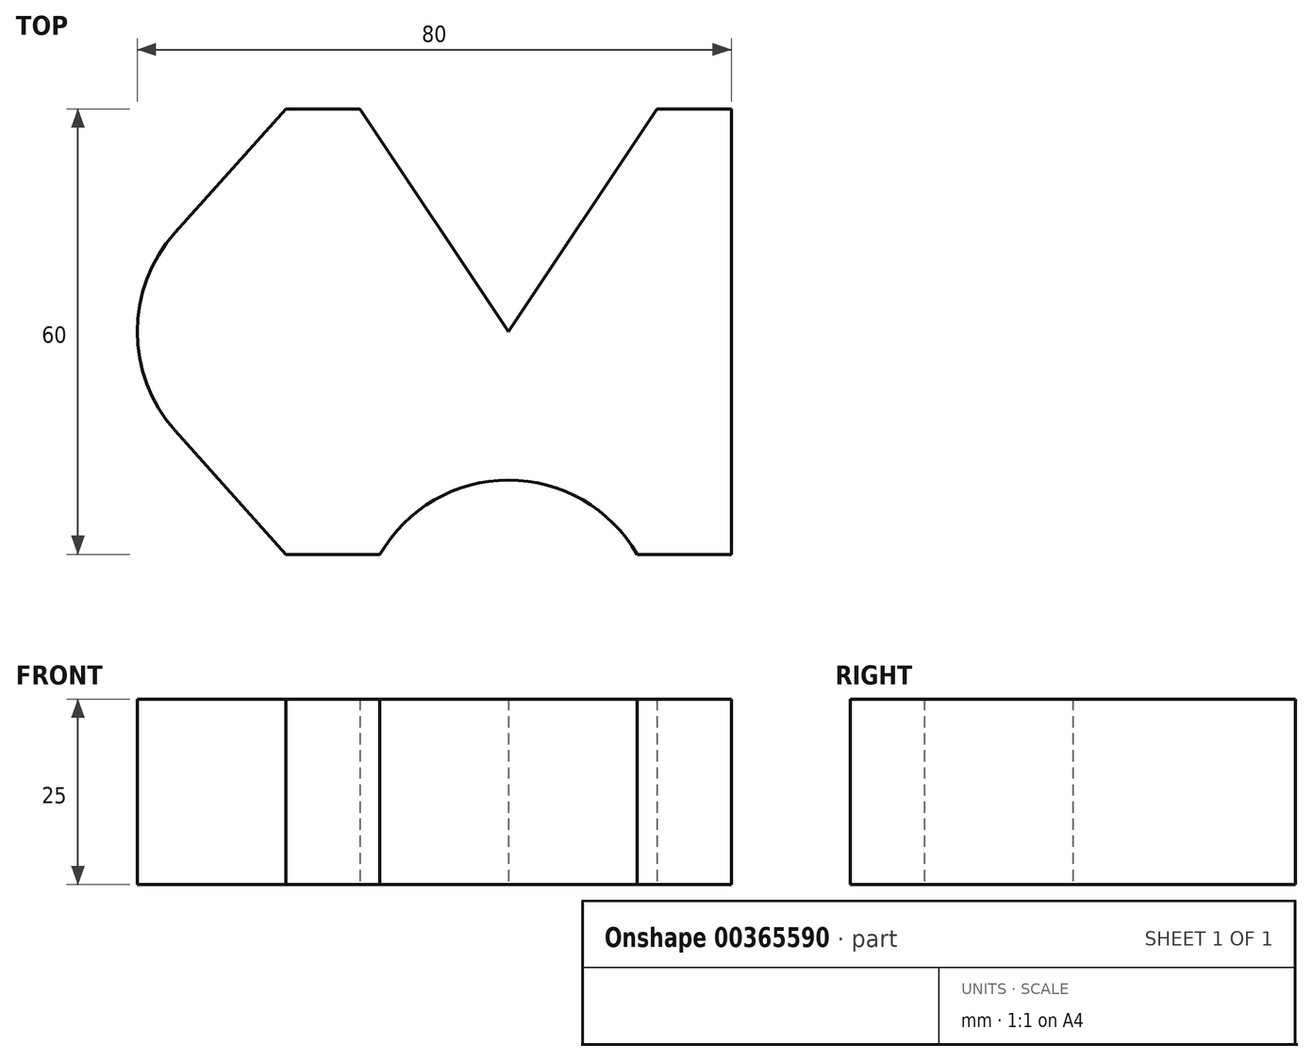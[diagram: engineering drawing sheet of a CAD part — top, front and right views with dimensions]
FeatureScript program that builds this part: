
annotation { "Feature Type Name" : "Feature", "Feature Type Description" : "" }
export const myFeature = defineFeature(function(context is Context, id is Id, definition is map)
    precondition{}
    {
        {
            var Q0;
            Q0=qCreatedBy(makeId("Top.planeOp"),FACE);
            var sketch = newSketch(context, id + "F0", { "sketchPlane" : qUnion([Q0])});
            skLineSegment(sketch, "E0", {"start": v(0, 0) * mm, "end": v(20, 30) * mm});
            skLineSegment(sketch, "E1", {"start": v(20, 30) * mm, "end": v(30, 30) * mm});
            skLineSegment(sketch, "E2", {"start": v(30, 30) * mm, "end": v(30, -30) * mm});
            skLineSegment(sketch, "E3", {"start": v(-17.32, -30) * mm, "end": v(-30, -30) * mm});
            skLineSegment(sketch, "E4", {"start": v(-30, -30) * mm, "end": v(-44.9, -13.33) * mm});
            skArc(sketch, "E5", {"start": v(-44.9, 13.33) * mm, "mid": v(-50, 0) * mm, "end": v(-44.9, -13.33) * mm});
            skLineSegment(sketch, "E6", {"start": v(-44.9, 13.33) * mm, "end": v(-30, 30) * mm});
            skLineSegment(sketch, "E7", {"start": v(-30, 30) * mm, "end": v(-20, 30) * mm});
            skLineSegment(sketch, "E8", {"start": v(-20, 30) * mm, "end": v(0, 0) * mm});
            skArc(sketch, "E9", {"start": v(17.32, -30) * mm, "mid": v(0, -20) * mm, "end": v(-17.32, -30) * mm});
            skLineSegment(sketch, "E10", {"start": v(17.32, -30) * mm, "end": v(30, -30) * mm});
            skLineSegment(sketch, "E11", {"start": v(-30, 30) * mm, "end": v(-30, -30) * mm, "construction": true});
            skSolve(sketch);
        }
        {
            var Q0;
            Q0 = qSketchRegion(id + "F0", true);
            extrude(context, id + "F1", {"entities" : qUnion([Q0]), "depth" : 25 * mm});
        }
    });
